# Revit family: 307_4613999cdd7b489490dcd40d072a99
name_source: partatom
category: Pipe Accessories
units: mm (PartAtom-declared; Revit-internal decimal feet)

## family parameters
Always vertical = Yes
Cut with Voids When Loaded = No
Part Type = Breaks Into
Round Connector Dimension = Use Diameter
Shared = No
Work Plane-Based = No

## types (4) — shared parameters
Description = Hydraulic separator, female unions, air vent and drain valve
E12 = 10 mm  [stored 0.0328084 ft]
E12__ve = -10 mm  [stored -0.0328084 ft]
E2 = 48 mm
E3 = 19 mm  [stored 0.062336 ft]
E4 = 10 mm  [stored 0.0328084 ft]
EE = 8 mm  [stored 0.0262467 ft]
ER = 5 mm  [stored 0.0164042 ft]
FT = 15 mm  [stored 0.0492126 ft]
FT__ve = -15 mm  [stored -0.0492126 ft]
L1 = 15 mm  [stored 0.0492126 ft]
L1__ve = -15 mm  [stored -0.0492126 ft]
L2D = 201 mm
L2D_Min = 3048 mm
Manufacturer = FAR
NR = 7 mm  [stored 0.0229659 ft]
NR1 = 9 mm  [stored 0.0295276 ft]
QmdConnectorList = 301;D;302;D
R2 = 8 mm  [stored 0.0262467 ft]
RR3 = 15 mm  [stored 0.0492126 ft]
RT = 8 mm  [stored 0.0262467 ft]
W2D = 25 mm  [stored 0.082021 ft]
magiPartTypeId = 307
magiProductFamilyId = 4613999cdd7b489490dcd40d072a99

## per-type parameters (varying)
| type | B | C | CenSd_DM2_6 | CenSd_DM3_6 | CenSd_RT1_6 | CenSd_RT2_6 | D | DM2 | DM3 | G | G2 | G2__ve | H | HT1 | H__ve | LL | LM | R | RR | RT1 | RT2 | TR | TR1 | magiProductId |
| 2161 1 | 135 mm | 220 mm | 14 mm  [stored 0.0459318 ft] | 17 mm  [stored 0.0557743 ft] | 12 mm  [stored 0.0393701 ft] | 9 mm  [stored 0.0295276 ft] | 25 mm | 16 mm  [stored 0.0524934 ft] | 20 mm  [stored 0.0656168 ft] | 60 mm | 120 mm | -120 mm | 77 mm | 125 mm | -77 mm | 101 mm | 141 mm | 13 mm  [stored 0.0426509 ft] | 12 mm  [stored 0.0393701 ft] | 14 mm  [stored 0.0459318 ft] | 11 mm | 21 mm  [stored 0.0688976 ft] | 27 mm  [stored 0.0885827 ft] | da555b7985444e7baef8a66cbeeef3 |
| 2161 112 | 155 mm | 260 mm | 23 mm | 28 mm | 16 mm  [stored 0.0524934 ft] | 12 mm  [stored 0.0393701 ft] | 40 mm | 26 mm | 32 mm | 75 mm | 150 mm | -150 mm | 91 mm | 145 mm | -91 mm | 132 mm | 204 mm | 20 mm  [stored 0.0656168 ft] | 15 mm  [stored 0.0492126 ft] | 18 mm | 14 mm  [stored 0.0459318 ft] | 26 mm | 34 mm  [stored 0.111549 ft] | b5faa296af4049c9aea8528f049d89 |
| 2161 114 | 145 mm | 240 mm | 18 mm | 22 mm | 14 mm  [stored 0.0459318 ft] | 10 mm  [stored 0.0328084 ft] | 32 mm | 21 mm  [stored 0.0688976 ft] | 26 mm | 65 mm | 130 mm | -130 mm | 81 mm | 135 mm | -81 mm | 118 mm | 176 mm | 16 mm  [stored 0.0524934 ft] | 13 mm  [stored 0.0426509 ft] | 16 mm  [stored 0.0524934 ft] | 12 mm  [stored 0.0393701 ft] | 23 mm | 29 mm | f38e94c4566840a985c9f7a9fe6514 |
| 2161 2 | 185 mm | 320 mm | 28 mm | 35 mm | 18 mm | 13 mm  [stored 0.0426509 ft] | 50 mm | 33 mm | 40 mm  [stored 0.131234 ft] | 85 mm | 170 mm | -170 mm  [stored -0.557743 ft] | 101 mm | 175 mm | -101 mm  [stored -0.331365 ft] | 168 mm | 275 mm | 25 mm  [stored 0.082021 ft] | 17 mm  [stored 0.0557743 ft] | 20 mm  [stored 0.0656168 ft] | 15 mm  [stored 0.0492126 ft] | 30 mm  [stored 0.0984252 ft] | 38 mm | b220c5fcef844040a3b514db8edb1e |

note: column(s) folded — value = type name in every type: MC Product Code

note: [stored X ft] marks values corroborated as IEEE doubles in the binary element streams (Revit-internal decimal feet)

## geometry (parser evidence)
native form markers: Sweep x3
no freeform markers — native parametric forms only
